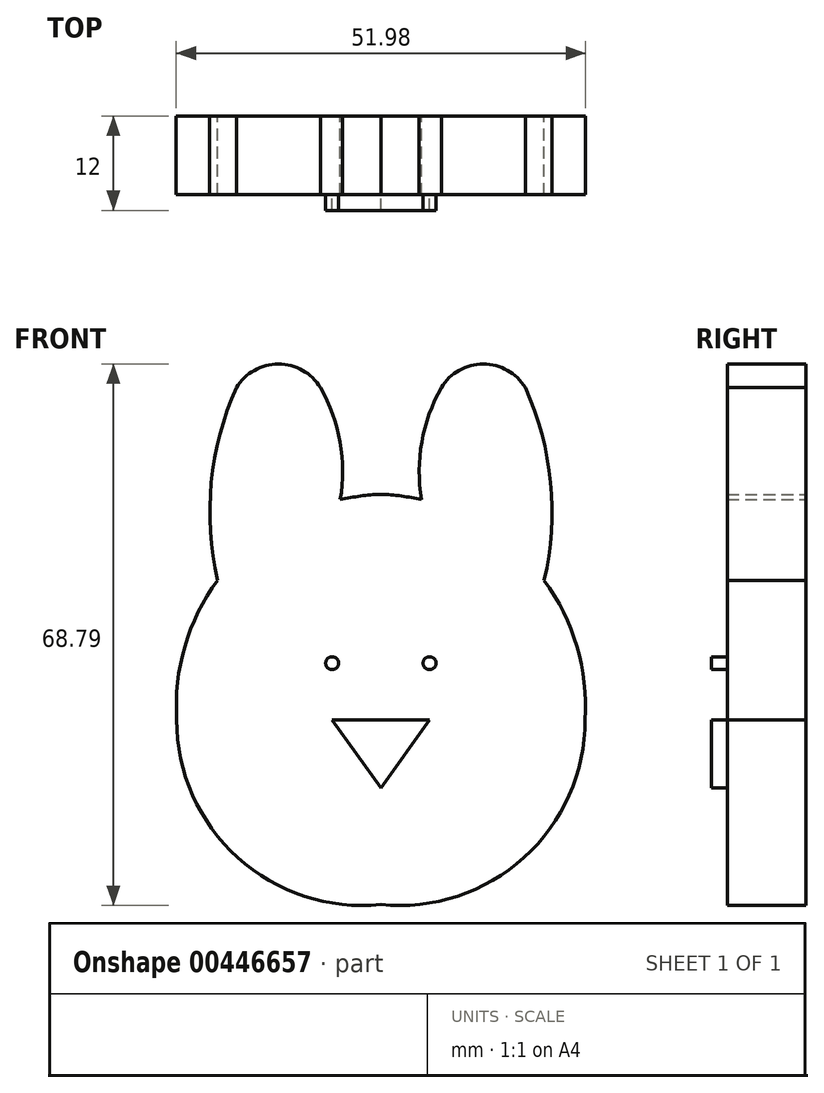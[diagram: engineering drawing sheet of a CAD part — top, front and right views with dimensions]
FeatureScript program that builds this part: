
annotation { "Feature Type Name" : "Feature", "Feature Type Description" : "" }
export const myFeature = defineFeature(function(context is Context, id is Id, definition is map)
    precondition{}
    {
        {
            var Q0;
            Q0=qCreatedBy(makeId("Front.planeOp"),FACE);
            var sketch = newSketch(context, id + "F0", { "sketchPlane" : qUnion([Q0])});
            skArc(sketch, "E0", {"start": v(-25.94, 0) * mm, "mid": v(-18.18, -17.5) * mm, "end": v(0, -23.46) * mm});
            skArc(sketch, "E1", {"start": v(0, 28.65) * mm, "mid": v(-19.03, 19.82) * mm, "end": v(-25.94, 0) * mm});
            skArc(sketch, "E2.MirrorCS", {"start": v(0, 28.65) * mm, "mid": v(19.03, 19.82) * mm, "end": v(25.94, 0) * mm});
            skArc(sketch, "E3.MirrorCS", {"start": v(25.94, 0) * mm, "mid": v(18.18, -17.5) * mm, "end": v(0, -23.46) * mm});
            skArc(sketch, "E4", {"start": v(-18.35, 42.2) * mm, "mid": v(-21.55, 30.16) * mm, "end": v(-20.74, 17.72) * mm});
            skArc(sketch, "E5", {"start": v(-5.16, 27.97) * mm, "mid": v(-5.2, 35.3) * mm, "end": v(-7.67, 42.2) * mm});
            skArc(sketch, "E6", {"start": v(-7.67, 42.2) * mm, "mid": v(-13.01, 45.2) * mm, "end": v(-18.35, 42.2) * mm});
            skArc(sketch, "E7.MirrorCS", {"start": v(5.16, 27.97) * mm, "mid": v(5.2, 35.3) * mm, "end": v(7.67, 42.2) * mm});
            skArc(sketch, "E8.MirrorCS", {"start": v(7.67, 42.2) * mm, "mid": v(13.01, 45.2) * mm, "end": v(18.35, 42.2) * mm});
            skArc(sketch, "E9.MirrorCS", {"start": v(18.35, 42.2) * mm, "mid": v(21.55, 30.16) * mm, "end": v(20.74, 17.72) * mm});
            skPoint(sketch, "E10", {"position": v(6.2, 8.3) * mm});
            skSolve(sketch);
        }
        {
            var Q0;
            Q0 = qSketchRegion(id + "F0", true);
            extrude(context, id + "F1", {"entities" : qUnion([Q0]), "depth" : 10 * mm});
        }
        {
            var Q0;
            Q0=makeQuery(id+"F1.opExtrude","CAP_FACE",FACE,{"disambiguationData":[OSD([sQuery(id+"F0.wireOp",EDGE,"E0"),sQuery(id+"F0.wireOp",EDGE,"E1"),sQuery(id+"F0.wireOp",EDGE,"E2.MirrorCS"),sQuery(id+"F0.wireOp",EDGE,"E3.MirrorCS"),sQuery(id+"F0.wireOp",EDGE,"E4"),sQuery(id+"F0.wireOp",EDGE,"E5"),sQuery(id+"F0.wireOp",EDGE,"E6"),sQuery(id+"F0.wireOp",EDGE,"E7.MirrorCS"),sQuery(id+"F0.wireOp",EDGE,"E8.MirrorCS"),sQuery(id+"F0.wireOp",EDGE,"E9.MirrorCS")])],"isStart":false});
            var sketch = newSketch(context, id + "F2", { "sketchPlane" : qUnion([Q0])});
            skLineSegment(sketch, "E11", {"start": v(0, 0) * mm, "end": v(-6.18, 0) * mm});
            skLineSegment(sketch, "E12", {"start": v(-6.18, 0) * mm, "end": v(0, -8.66) * mm});
            skCircle(sketch, "E13", {"center": v(-6.18, 7.2) * mm, "radius": 0.82 * mm});
            skCircle(sketch, "E14.MirrorC", {"center": v(6.18, 7.2) * mm, "radius": 0.82 * mm});
            skLineSegment(sketch, "E15.MirrorCS", {"start": v(0, 0) * mm, "end": v(6.18, 0) * mm});
            skLineSegment(sketch, "E16.MirrorCS", {"start": v(6.18, 0) * mm, "end": v(0, -8.66) * mm});
            skSolve(sketch);
        }
        {
            var Q0;
            Q0 = qSketchRegion(id + "F2", true);
            extrude(context, id + "F3", {"entities" : qUnion([Q0]), "operationType" : NewBodyOperationType.ADD, "depth" : 2 * mm});
        }
    });
